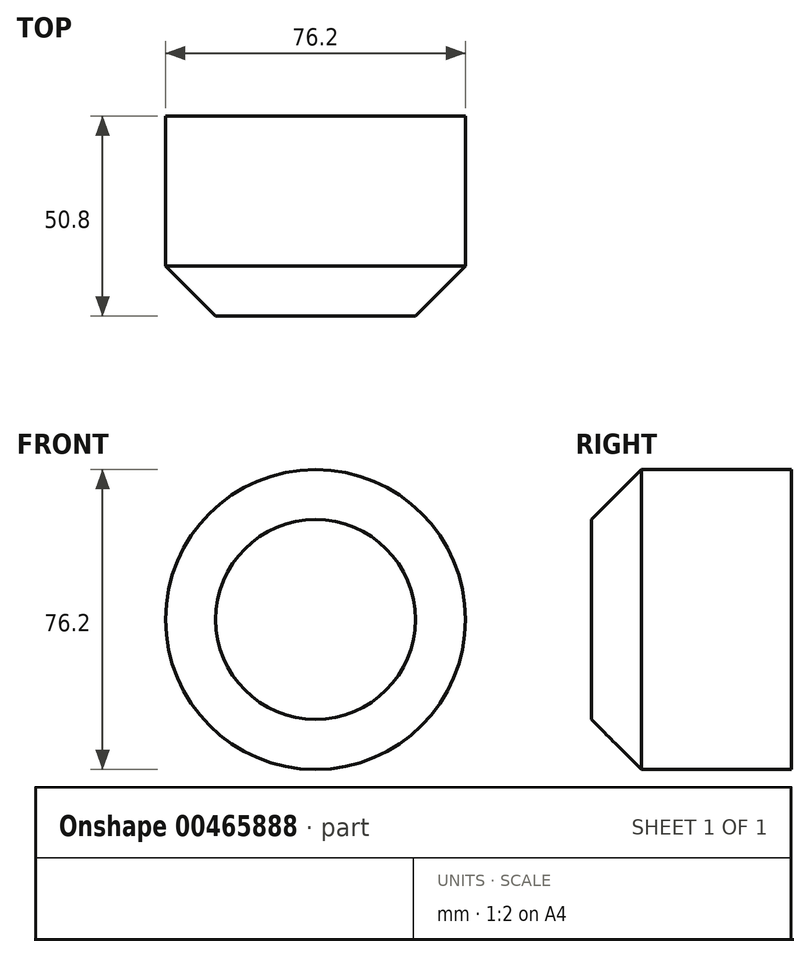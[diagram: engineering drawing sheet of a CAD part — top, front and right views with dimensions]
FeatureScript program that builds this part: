
annotation { "Feature Type Name" : "Feature", "Feature Type Description" : "" }
export const myFeature = defineFeature(function(context is Context, id is Id, definition is map)
    precondition{}
    {
        {
            var Q0;
            Q0=qCreatedBy(makeId("Front.planeOp"),FACE);
            var sketch = newSketch(context, id + "F0", { "sketchPlane" : qUnion([Q0])});
            skCircle(sketch, "E0", {"center": v(0, 0) * mm, "radius": 38.1 * mm});
            skSolve(sketch);
        }
        {
            var Q0;
            Q0=makeQuery(id+"F0.imprint","IMPRINT",FACE,{"disambiguationData":[TD([[makeQuery(id+"F0.imprint","IMPRINT",EDGE,{"derivedFrom":sQuery(id+"F0.wireOp",EDGE,"E0")}),1.0]])]});
            extrude(context, id + "F1", {"entities" : qUnion([Q0]), "depth" : 50.8 * mm, "offsetDistance" : 25.4 * mm});
        }
        {
            var Q0;
            Q0=makeQuery(id+"F1.opExtrude","CAP_EDGE",EDGE,{"disambiguationData":[OSD([sQuery(id+"F0.wireOp",EDGE,"E0")])],"isStart":false});
            chamfer(context, id + "F2", {"entities" : qUnion([Q0]), "width" : 12.7 * mm, "tangentPropagation" : true});
        }
    });
